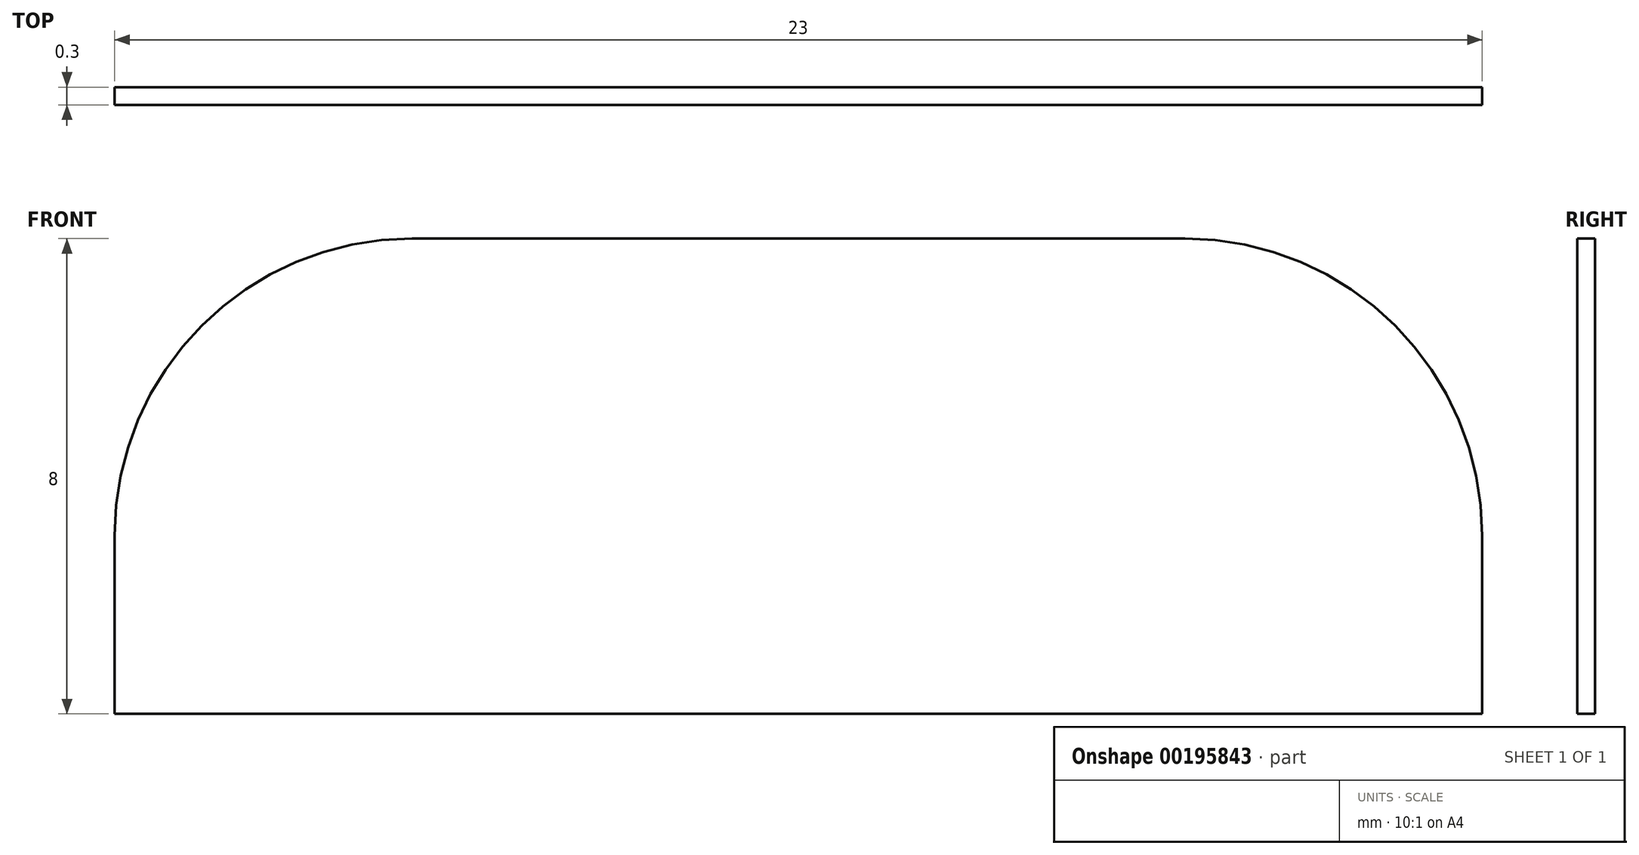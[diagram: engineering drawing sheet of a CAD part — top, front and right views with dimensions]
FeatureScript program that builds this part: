
annotation { "Feature Type Name" : "Feature", "Feature Type Description" : "" }
export const myFeature = defineFeature(function(context is Context, id is Id, definition is map)
    precondition{}
    {
        {
            var Q0;
            Q0=qCreatedBy(makeId("Front.planeOp"),FACE);
            var sketch = newSketch(context, id + "F0", { "sketchPlane" : qUnion([Q0])});
            skLineSegment(sketch, "E0.bottom", {"start": v(0, 0) * mm, "end": v(23, 0) * mm});
            skLineSegment(sketch, "E0.top", {"start": v(5, 8) * mm, "end": v(18, 8) * mm});
            skLineSegment(sketch, "E0.left", {"start": v(0, 0) * mm, "end": v(0, 3) * mm});
            skLineSegment(sketch, "E0.right", {"start": v(23, 0) * mm, "end": v(23, 3) * mm});
            skPoint(sketch, "E1.visualSharp", {"position": v(0, 8) * mm});
            skArc(sketch, "E1.filletArc", {"start": v(5, 8) * mm, "mid": v(1.46, 6.54) * mm, "end": v(0, 3) * mm});
            skPoint(sketch, "E2.visualSharp", {"position": v(23, 8) * mm});
            skArc(sketch, "E2.filletArc", {"start": v(23, 3) * mm, "mid": v(21.54, 6.54) * mm, "end": v(18, 8) * mm});
            skSolve(sketch);
        }
        {
            var Q0;
            Q0=makeQuery(id+"F0.imprint","IMPRINT",FACE,{"disambiguationData":[TD([[makeQuery(id+"F0.imprint","IMPRINT",EDGE,{"derivedFrom":sQuery(id+"F0.wireOp",EDGE,"E0.bottom")}),1.0]])]});
            extrude(context, id + "F1", {"entities" : qUnion([Q0]), "depth" : .3 * mm});
        }
    });
